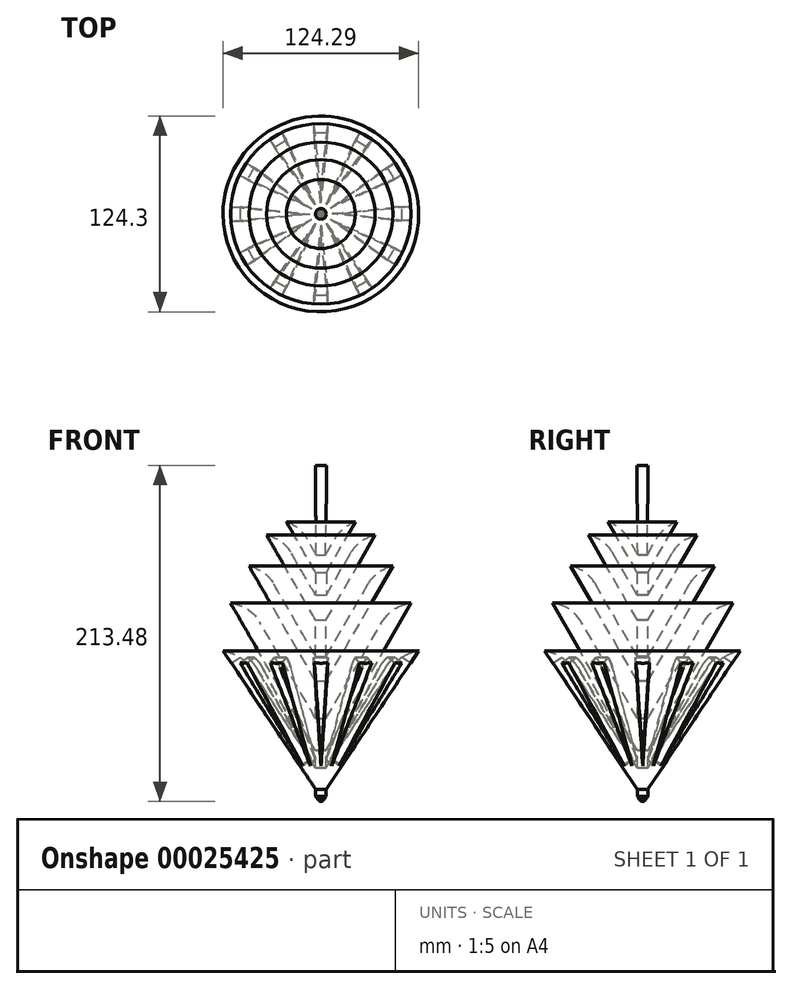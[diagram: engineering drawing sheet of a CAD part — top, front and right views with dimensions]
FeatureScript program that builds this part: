
annotation { "Feature Type Name" : "Feature", "Feature Type Description" : "" }
export const myFeature = defineFeature(function(context is Context, id is Id, definition is map)
    precondition{}
    {
        {
            var Q0;
            Q0=qCreatedBy(makeId("Front.planeOp"),FACE);
            var sketch = newSketch(context, id + "F0", { "sketchPlane" : qUnion([Q0])});
            skLineSegment(sketch, "E0", {"start": v(27.65, 100.39) * mm, "end": v(28.04, 56.23) * mm});
            skLineSegment(sketch, "E1", {"start": v(28.04, 56.23) * mm, "end": v(13.58, 81.61) * mm});
            skLineSegment(sketch, "E2", {"start": v(13.58, 81.61) * mm, "end": v(9.14, 77.17) * mm});
            skLineSegment(sketch, "E3", {"start": v(9.14, 77.17) * mm, "end": v(27.63, 45.14) * mm});
            skLineSegment(sketch, "E4", {"start": v(27.63, 45.14) * mm, "end": v(27.63, 30.64) * mm});
            skLineSegment(sketch, "E5", {"start": v(27.63, 30.64) * mm, "end": v(2.32, 74.47) * mm});
            skLineSegment(sketch, "E6", {"start": v(2.32, 74.47) * mm, "end": v(-3.4, 68.75) * mm});
            skLineSegment(sketch, "E7", {"start": v(-3.4, 68.75) * mm, "end": v(27.7, 14.86) * mm});
            skLineSegment(sketch, "E8", {"start": v(27.7, 14.86) * mm, "end": v(27.72, -8.4) * mm});
            skLineSegment(sketch, "E9", {"start": v(27.72, -8.4) * mm, "end": v(-8.81, 54.88) * mm});
            skLineSegment(sketch, "E10", {"start": v(-8.81, 54.88) * mm, "end": v(-14.6, 49.1) * mm});
            skLineSegment(sketch, "E11", {"start": v(-14.6, 49.1) * mm, "end": v(27.73, -23.97) * mm});
            skLineSegment(sketch, "E12", {"start": v(27.73, -23.97) * mm, "end": v(27.75, -47.71) * mm});
            skLineSegment(sketch, "E13", {"start": v(27.75, -47.71) * mm, "end": v(-18.99, 32.78) * mm});
            skLineSegment(sketch, "E14", {"start": v(-18.99, 32.78) * mm, "end": v(-26.26, 25.51) * mm});
            skLineSegment(sketch, "E15", {"start": v(-26.26, 25.51) * mm, "end": v(27.76, -68.05) * mm});
            skLineSegment(sketch, "E16", {"start": v(27.76, -68.05) * mm, "end": v(27.77, -79.08) * mm});
            skLineSegment(sketch, "E17", {"start": v(27.77, -79.08) * mm, "end": v(-25.1, 1.04) * mm});
            skLineSegment(sketch, "E18", {"start": v(-25.1, 1.04) * mm, "end": v(-31.07, -4.74) * mm});
            skLineSegment(sketch, "E19", {"start": v(-31.07, -4.74) * mm, "end": v(27.62, -92.51) * mm});
            skLineSegment(sketch, "E20", {"start": v(27.62, -92.51) * mm, "end": v(27.78, -92.75) * mm});
            skLineSegment(sketch, "E21", {"start": v(27.78, -92.75) * mm, "end": v(27.78, -97.16) * mm});
            skLineSegment(sketch, "E22", {"start": v(27.78, -97.16) * mm, "end": v(27.87, -97.3) * mm});
            skLineSegment(sketch, "E23", {"start": v(27.87, -97.3) * mm, "end": v(28.1, -97.65) * mm});
            skLineSegment(sketch, "E24", {"start": v(28.1, -97.65) * mm, "end": v(28.43, -98.16) * mm});
            skLineSegment(sketch, "E25", {"start": v(28.43, -98.16) * mm, "end": v(28.83, -98.73) * mm});
            skLineSegment(sketch, "E26", {"start": v(28.83, -98.73) * mm, "end": v(29.26, -99.31) * mm});
            skLineSegment(sketch, "E27", {"start": v(29.26, -99.31) * mm, "end": v(29.67, -99.82) * mm});
            skLineSegment(sketch, "E28", {"start": v(29.67, -99.82) * mm, "end": v(30.04, -100.19) * mm});
            skLineSegment(sketch, "E29", {"start": v(30.04, -100.19) * mm, "end": v(30.31, -100.34) * mm});
            skLineSegment(sketch, "E30", {"start": v(30.31, -100.34) * mm, "end": v(30.93, -100.38) * mm});
            skLineSegment(sketch, "E31", {"start": v(30.93, -100.38) * mm, "end": v(31.07, -100.39) * mm});
            skLineSegment(sketch, "E32", {"start": v(31.07, -100.39) * mm, "end": v(31.07, 100.39) * mm});
            skLineSegment(sketch, "E33", {"start": v(31.07, 100.39) * mm, "end": v(27.65, 100.39) * mm});
            skSolve(sketch);
        }
        {
            var Q0;
            Q0=makeQuery(id+"F0.imprint","IMPRINT",FACE,{"disambiguationData":[TD([[makeQuery(id+"F0.imprint","IMPRINT",EDGE,{"derivedFrom":sQuery(id+"F0.wireOp",EDGE,"E0")}),1.0]])]});
            var Q1;
            Q1=sQuery(id+"F0.wireOp",EDGE,"E32");
            revolve(context, id + "F1", {"entities" : qUnion([Q0]), "axis" : qUnion([Q1]), "revolveType" : RevolveType.FULL});
        }
        {
            var Q0;
            Q0=qCreatedBy(makeId("Front.planeOp"),FACE);
            var sketch = newSketch(context, id + "F2", { "sketchPlane" : qUnion([Q0])});
            skLineSegment(sketch, "E34", {"start": v(-36.31, 0) * mm, "end": v(-40.74, -78.3) * mm});
            skLineSegment(sketch, "E35", {"start": v(-40.74, -78.3) * mm, "end": v(-45.17, 0) * mm});
            skLineSegment(sketch, "E36", {"start": v(-45.17, 0) * mm, "end": v(-36.31, 0) * mm});
            skSolve(sketch);
        }
        {
            var Q0;
            Q0=makeQuery(id+"F2.imprint","IMPRINT",FACE,{"disambiguationData":[TD([[makeQuery(id+"F2.imprint","IMPRINT",EDGE,{"derivedFrom":sQuery(id+"F2.wireOp",EDGE,"E34")}),-1.0]])]});
            extrude(context, id + "F3", {"entities" : qUnion([Q0]), "depth" : 25.4 * mm});
        }
        {
            var Q0;
            Q0=makeQuery(id+"F3.opExtrude","SWEPT_BODY",BODY,{"disambiguationData":[OSD([sQuery(id+"F2.wireOp",EDGE,"E34"),sQuery(id+"F2.wireOp",EDGE,"E35"),sQuery(id+"F2.wireOp",EDGE,"E36")])]});
            var Q1;
            Q1=makeQuery(id+"F3.opExtrude","CAP_EDGE",EDGE,{"disambiguationData":[OSD([sQuery(id+"F2.wireOp",EDGE,"E36")])],"isStart":false});
            transform(context, id + "F4", {"entities" : qUnion([Q0]), "transformType" : TransformType.ROTATION, "transformAxis" : qUnion([Q1]), "angle" : 33.3 * degree, "makeCopy" : false});
        }
        {
            var Q0;
            Q0=makeQuery(id+"F3.opExtrude","SWEPT_BODY",BODY,{"disambiguationData":[OSD([sQuery(id+"F2.wireOp",EDGE,"E34"),sQuery(id+"F2.wireOp",EDGE,"E35"),sQuery(id+"F2.wireOp",EDGE,"E36")])]});
            transform(context, id + "F5", {"entities" : qUnion([Q0]), "transformType" : TransformType.TRANSLATION_3D, "dx" : 71.92 * mm, "dy" : -43.25 * mm, "dz" : -20.33 * mm, "makeCopy" : false});
        }
        {
            var Q0;
            Q0=makeQuery(id+"F3.opExtrude","SWEPT_BODY",BODY,{"disambiguationData":[OSD([sQuery(id+"F2.wireOp",EDGE,"E34"),sQuery(id+"F2.wireOp",EDGE,"E35"),sQuery(id+"F2.wireOp",EDGE,"E36")])]});
            var Q1;
            Q1=makeQuery(id+"F1.opRevolve","SWEPT_BODY",BODY,{"disambiguationData":[OSD([sQuery(id+"F0.wireOp",EDGE,"E0"),sQuery(id+"F0.wireOp",EDGE,"E1"),sQuery(id+"F0.wireOp",EDGE,"E2"),sQuery(id+"F0.wireOp",EDGE,"E3"),sQuery(id+"F0.wireOp",EDGE,"E4"),sQuery(id+"F0.wireOp",EDGE,"E5"),sQuery(id+"F0.wireOp",EDGE,"E6"),sQuery(id+"F0.wireOp",EDGE,"E7"),sQuery(id+"F0.wireOp",EDGE,"E8"),sQuery(id+"F0.wireOp",EDGE,"E9"),sQuery(id+"F0.wireOp",EDGE,"E10"),sQuery(id+"F0.wireOp",EDGE,"E11"),sQuery(id+"F0.wireOp",EDGE,"E12"),sQuery(id+"F0.wireOp",EDGE,"E13"),sQuery(id+"F0.wireOp",EDGE,"E14"),sQuery(id+"F0.wireOp",EDGE,"E15"),sQuery(id+"F0.wireOp",EDGE,"E16"),sQuery(id+"F0.wireOp",EDGE,"E17"),sQuery(id+"F0.wireOp",EDGE,"E18"),sQuery(id+"F0.wireOp",EDGE,"E19"),sQuery(id+"F0.wireOp",EDGE,"E20"),sQuery(id+"F0.wireOp",EDGE,"E21"),sQuery(id+"F0.wireOp",EDGE,"E22"),sQuery(id+"F0.wireOp",EDGE,"E23"),sQuery(id+"F0.wireOp",EDGE,"E24"),sQuery(id+"F0.wireOp",EDGE,"E25"),sQuery(id+"F0.wireOp",EDGE,"E26"),sQuery(id+"F0.wireOp",EDGE,"E27"),sQuery(id+"F0.wireOp",EDGE,"E28"),sQuery(id+"F0.wireOp",EDGE,"E29"),sQuery(id+"F0.wireOp",EDGE,"E30"),sQuery(id+"F0.wireOp",EDGE,"E31"),sQuery(id+"F0.wireOp",EDGE,"E32"),sQuery(id+"F0.wireOp",EDGE,"E33")])]});
            booleanBodies(context, id + "F6", {"operationType" : BooleanOperationType.SUBTRACTION, "tools" : qUnion([Q0]), "targets" : qUnion([Q1]), "keepTools" : true});
        }
        {
            var Q0;
            Q0=makeQuery(id+"F3.opExtrude","SWEPT_BODY",BODY,{"disambiguationData":[OSD([sQuery(id+"F2.wireOp",EDGE,"E34"),sQuery(id+"F2.wireOp",EDGE,"E35"),sQuery(id+"F2.wireOp",EDGE,"E36")])]});
            var Q1;
            Q1=makeQuery(id+"F1.opRevolve","SWEPT_EDGE",EDGE,{"disambiguationData":[OSD([sQuery(id+"F0.wireOp",EDGE,"E13"),sQuery(id+"F0.wireOp",EDGE,"E14")])]});
            circularPattern(context, id + "F7", {"entities" : qUnion([Q0]), "axis" : qUnion([Q1]), "angle" : 30 * degree, "instanceCount" : 12});
        }
        {
            var Q0;
            Q0=makeQuery(id+"F7.opPattern","COPY",BODY,{"derivedFrom":makeQuery(id+"F3.opExtrude","SWEPT_BODY",BODY,{"disambiguationData":[OSD([sQuery(id+"F2.wireOp",EDGE,"E34"),sQuery(id+"F2.wireOp",EDGE,"E35"),sQuery(id+"F2.wireOp",EDGE,"E36")])]}),"instanceName":"11"});
            var Q1;
            Q1=makeQuery(id+"F7.opPattern","COPY",BODY,{"derivedFrom":makeQuery(id+"F3.opExtrude","SWEPT_BODY",BODY,{"disambiguationData":[OSD([sQuery(id+"F2.wireOp",EDGE,"E34"),sQuery(id+"F2.wireOp",EDGE,"E35"),sQuery(id+"F2.wireOp",EDGE,"E36")])]}),"instanceName":"10"});
            var Q2;
            Q2=makeQuery(id+"F7.opPattern","COPY",BODY,{"derivedFrom":makeQuery(id+"F3.opExtrude","SWEPT_BODY",BODY,{"disambiguationData":[OSD([sQuery(id+"F2.wireOp",EDGE,"E34"),sQuery(id+"F2.wireOp",EDGE,"E35"),sQuery(id+"F2.wireOp",EDGE,"E36")])]}),"instanceName":"9"});
            var Q3;
            Q3=makeQuery(id+"F3.opExtrude","SWEPT_BODY",BODY,{"disambiguationData":[OSD([sQuery(id+"F2.wireOp",EDGE,"E34"),sQuery(id+"F2.wireOp",EDGE,"E35"),sQuery(id+"F2.wireOp",EDGE,"E36")])]});
            var Q4;
            Q4=makeQuery(id+"F7.opPattern","COPY",BODY,{"derivedFrom":makeQuery(id+"F3.opExtrude","SWEPT_BODY",BODY,{"disambiguationData":[OSD([sQuery(id+"F2.wireOp",EDGE,"E34"),sQuery(id+"F2.wireOp",EDGE,"E35"),sQuery(id+"F2.wireOp",EDGE,"E36")])]}),"instanceName":"1"});
            var Q5;
            Q5=makeQuery(id+"F7.opPattern","COPY",BODY,{"derivedFrom":makeQuery(id+"F3.opExtrude","SWEPT_BODY",BODY,{"disambiguationData":[OSD([sQuery(id+"F2.wireOp",EDGE,"E34"),sQuery(id+"F2.wireOp",EDGE,"E35"),sQuery(id+"F2.wireOp",EDGE,"E36")])]}),"instanceName":"2"});
            var Q6;
            Q6=makeQuery(id+"F7.opPattern","COPY",BODY,{"derivedFrom":makeQuery(id+"F3.opExtrude","SWEPT_BODY",BODY,{"disambiguationData":[OSD([sQuery(id+"F2.wireOp",EDGE,"E34"),sQuery(id+"F2.wireOp",EDGE,"E35"),sQuery(id+"F2.wireOp",EDGE,"E36")])]}),"instanceName":"3"});
            var Q7;
            Q7=makeQuery(id+"F7.opPattern","COPY",BODY,{"derivedFrom":makeQuery(id+"F3.opExtrude","SWEPT_BODY",BODY,{"disambiguationData":[OSD([sQuery(id+"F2.wireOp",EDGE,"E34"),sQuery(id+"F2.wireOp",EDGE,"E35"),sQuery(id+"F2.wireOp",EDGE,"E36")])]}),"instanceName":"4"});
            var Q8;
            Q8=makeQuery(id+"F7.opPattern","COPY",BODY,{"derivedFrom":makeQuery(id+"F3.opExtrude","SWEPT_BODY",BODY,{"disambiguationData":[OSD([sQuery(id+"F2.wireOp",EDGE,"E34"),sQuery(id+"F2.wireOp",EDGE,"E35"),sQuery(id+"F2.wireOp",EDGE,"E36")])]}),"instanceName":"5"});
            var Q9;
            Q9=makeQuery(id+"F7.opPattern","COPY",BODY,{"derivedFrom":makeQuery(id+"F3.opExtrude","SWEPT_BODY",BODY,{"disambiguationData":[OSD([sQuery(id+"F2.wireOp",EDGE,"E34"),sQuery(id+"F2.wireOp",EDGE,"E35"),sQuery(id+"F2.wireOp",EDGE,"E36")])]}),"instanceName":"6"});
            var Q10;
            Q10=makeQuery(id+"F7.opPattern","COPY",BODY,{"derivedFrom":makeQuery(id+"F3.opExtrude","SWEPT_BODY",BODY,{"disambiguationData":[OSD([sQuery(id+"F2.wireOp",EDGE,"E34"),sQuery(id+"F2.wireOp",EDGE,"E35"),sQuery(id+"F2.wireOp",EDGE,"E36")])]}),"instanceName":"7"});
            var Q11;
            Q11=makeQuery(id+"F7.opPattern","COPY",BODY,{"derivedFrom":makeQuery(id+"F3.opExtrude","SWEPT_BODY",BODY,{"disambiguationData":[OSD([sQuery(id+"F2.wireOp",EDGE,"E34"),sQuery(id+"F2.wireOp",EDGE,"E35"),sQuery(id+"F2.wireOp",EDGE,"E36")])]}),"instanceName":"8"});
            var Q12;
            Q12=makeQuery(id+"F1.opRevolve","SWEPT_BODY",BODY,{"disambiguationData":[OSD([sQuery(id+"F0.wireOp",EDGE,"E0"),sQuery(id+"F0.wireOp",EDGE,"E1"),sQuery(id+"F0.wireOp",EDGE,"E2"),sQuery(id+"F0.wireOp",EDGE,"E3"),sQuery(id+"F0.wireOp",EDGE,"E4"),sQuery(id+"F0.wireOp",EDGE,"E5"),sQuery(id+"F0.wireOp",EDGE,"E6"),sQuery(id+"F0.wireOp",EDGE,"E7"),sQuery(id+"F0.wireOp",EDGE,"E8"),sQuery(id+"F0.wireOp",EDGE,"E9"),sQuery(id+"F0.wireOp",EDGE,"E10"),sQuery(id+"F0.wireOp",EDGE,"E11"),sQuery(id+"F0.wireOp",EDGE,"E12"),sQuery(id+"F0.wireOp",EDGE,"E13"),sQuery(id+"F0.wireOp",EDGE,"E14"),sQuery(id+"F0.wireOp",EDGE,"E15"),sQuery(id+"F0.wireOp",EDGE,"E16"),sQuery(id+"F0.wireOp",EDGE,"E17"),sQuery(id+"F0.wireOp",EDGE,"E18"),sQuery(id+"F0.wireOp",EDGE,"E19"),sQuery(id+"F0.wireOp",EDGE,"E20"),sQuery(id+"F0.wireOp",EDGE,"E21"),sQuery(id+"F0.wireOp",EDGE,"E22"),sQuery(id+"F0.wireOp",EDGE,"E23"),sQuery(id+"F0.wireOp",EDGE,"E24"),sQuery(id+"F0.wireOp",EDGE,"E25"),sQuery(id+"F0.wireOp",EDGE,"E26"),sQuery(id+"F0.wireOp",EDGE,"E27"),sQuery(id+"F0.wireOp",EDGE,"E28"),sQuery(id+"F0.wireOp",EDGE,"E29"),sQuery(id+"F0.wireOp",EDGE,"E30"),sQuery(id+"F0.wireOp",EDGE,"E31"),sQuery(id+"F0.wireOp",EDGE,"E32"),sQuery(id+"F0.wireOp",EDGE,"E33")])]});
            booleanBodies(context, id + "F8", {"operationType" : BooleanOperationType.SUBTRACTION, "tools" : qUnion([Q0, Q1, Q2, Q3, Q4, Q5, Q6, Q7, Q8, Q9, Q10, Q11]), "targets" : qUnion([Q12])});
        }
        {
            var Q0;
            Q0=makeQuery(id+"F1.opRevolve","SWEPT_EDGE",EDGE,{"disambiguationData":[OSD([sQuery(id+"F0.wireOp",EDGE,"E9"),sQuery(id+"F0.wireOp",EDGE,"E10")])]});
            var Q1;
            Q1=makeQuery(id+"F1.opRevolve","SWEPT_EDGE",EDGE,{"disambiguationData":[OSD([sQuery(id+"F0.wireOp",EDGE,"E13"),sQuery(id+"F0.wireOp",EDGE,"E14")])]});
            var Q2;
            Q2=makeQuery(id+"F1.opRevolve","SWEPT_EDGE",EDGE,{"disambiguationData":[OSD([sQuery(id+"F0.wireOp",EDGE,"E17"),sQuery(id+"F0.wireOp",EDGE,"E18")])]});
            var Q3;
            Q3=makeQuery(id+"F1.opRevolve","SWEPT_EDGE",EDGE,{"disambiguationData":[OSD([sQuery(id+"F0.wireOp",EDGE,"E5"),sQuery(id+"F0.wireOp",EDGE,"E6")])]});
            var Q4;
            Q4=makeQuery(id+"F1.opRevolve","SWEPT_EDGE",EDGE,{"disambiguationData":[OSD([sQuery(id+"F0.wireOp",EDGE,"E1"),sQuery(id+"F0.wireOp",EDGE,"E2")])]});
            fillet(context, id + "F9", {"entities" : qUnion([Q0, Q1, Q2, Q3, Q4]), "radius" : 24.05 * mm, "tangentPropagation" : true, "allowEdgeOverflow" : false});
        }
        {
            var Q0;
            Q0=makeQuery(id+"F1.opRevolve","SWEPT_FACE",FACE,{"disambiguationData":[OSD([sQuery(id+"F0.wireOp",EDGE,"E33")])]});
            extrude(context, id + "F10", {"entities" : qUnion([Q0]), "operationType" : NewBodyOperationType.ADD, "depth" : 12.7 * mm});
        }
    });
